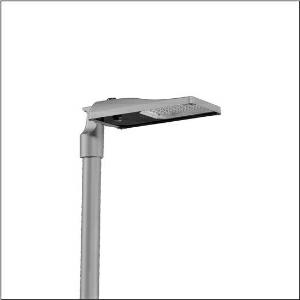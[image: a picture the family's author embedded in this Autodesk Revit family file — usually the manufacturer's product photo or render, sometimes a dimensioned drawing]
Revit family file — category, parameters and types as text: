
# Revit family: streetlight_sl_31_mini___st1_0a_5xh6d31t08ga_3ef0
name_source: partatom
category: Lighting Fixtures
units: mm (PartAtom-declared; Revit-internal decimal feet)

## family parameters
Cut with Voids When Loaded = No
Host = Face
Light Source = No
Part Type = Normal
Room Calculation Point = No
Round Connector Dimension = Use Diameter
Shared = No

## types (1)
- --- (1 x LED, 5880 lm, 39.3 W, 3000K)
    Apparent Load = 39 VA
    CIE Flux Codes = 37 72 97 100 100
    Color Rendering = 70
    Color Temperature = 3000K
    Default Elevation = 1800 mm
    Description = Streetlight SL 31 mini D4i, Desk-Remote mast luminaire for post-top, side-entry; light control with lens of PMMA; light distribution: ST1.0a, direct asymmetric distribution, for standard-compliant lighting for roads and squares; LED: luminous flux: 5.880lm, light colour: 730, colour temperature: 3000K; luminous efficacy: 149,6lm/W; control: pre-setting: logarithmic dimming characteristic, flexible luminous flux parameterisation, time-dependent luminous flux control, constant luminous flux control, power reduction, intelligent temperature release in ECG and LED module, overheat protection; luminaire housing, of diecast aluminium, Siteco® metallic grey (DB 702S), corrosivity category C5 high according to DIN EN ISO 12944; cover of toughened safety glass, transparent, opened without tools; mast flange of diecast aluminium, Siteco® metallic grey (DB 702S), spigot size: 76/60mm, mast flange included unmounted; with cable H07RN-F 2x 1.5mm², cable length: 6,5m, connection cable pre-assembled; mains connection: 220..240V, AC, 50/60Hz; power consumption (at start of service life): 39,3W / (at end of service life): 40,7W / (with reduced operation 50%): 18,1W; protection rating (complete): IP66; insulation class (complete): insulation class II (safety insulation); impact resistance: IK09; certification: CE, ENEC, ENEC+, VDE, UKCA, ZD4i; permissible operating ambient temperature for outdoor applications: -40..+50°C; packaging unit: 1 piece

Light Distribution: ST1.0a
    Height = 76 mm
    Lamp = 1 x LED
    Lamp Light Flux = 5880 lm
    Lamp Power = 39.3 W
    Lamp count = 1
    Length = 547 mm
    Luminous efficacy = 150 lm/W
    Manufacturer = Siteco
    ModVariant = No
    Model = 5XH6D31T08GA
    Number of Poles = 1
    OnlyDefault = Yes
    Power Factor = 1
    Product Name = Streetlight SL 31 mini | ST1.0a
    Product group = mast luminaire | pylon top
    ProductGroupID = 6100
    Protection Class = Protection class II
    Protection Degree = IP 66
    RLX_Detail_Level = 1
    RLX_Emergency_Light_Flux = 0 lm
    RLX_Emergency_Type = 0
    RLX_Emergency_Type_DB = No
    RlxData = <blob elided: 39697 chars, md5=2ec67032>
    Socket = socket
    Standby Power = 0 W
    System Light Flux = 5880 lm
    System Power = 39 W
    Type Comments = factory setting: luminous flux: 100 % | dim-lin: 254 | 798 mA
    Type Image = l_1300332.jpg
    URL = http://relux.com
    VarID = @adj_074307
    Voltage = 0 V
    Weight = 0.00 kg
    Width = 265 mm

## geometry (parser evidence)
native form markers: Blend x4, Sweep x9
no freeform markers — native parametric forms only
